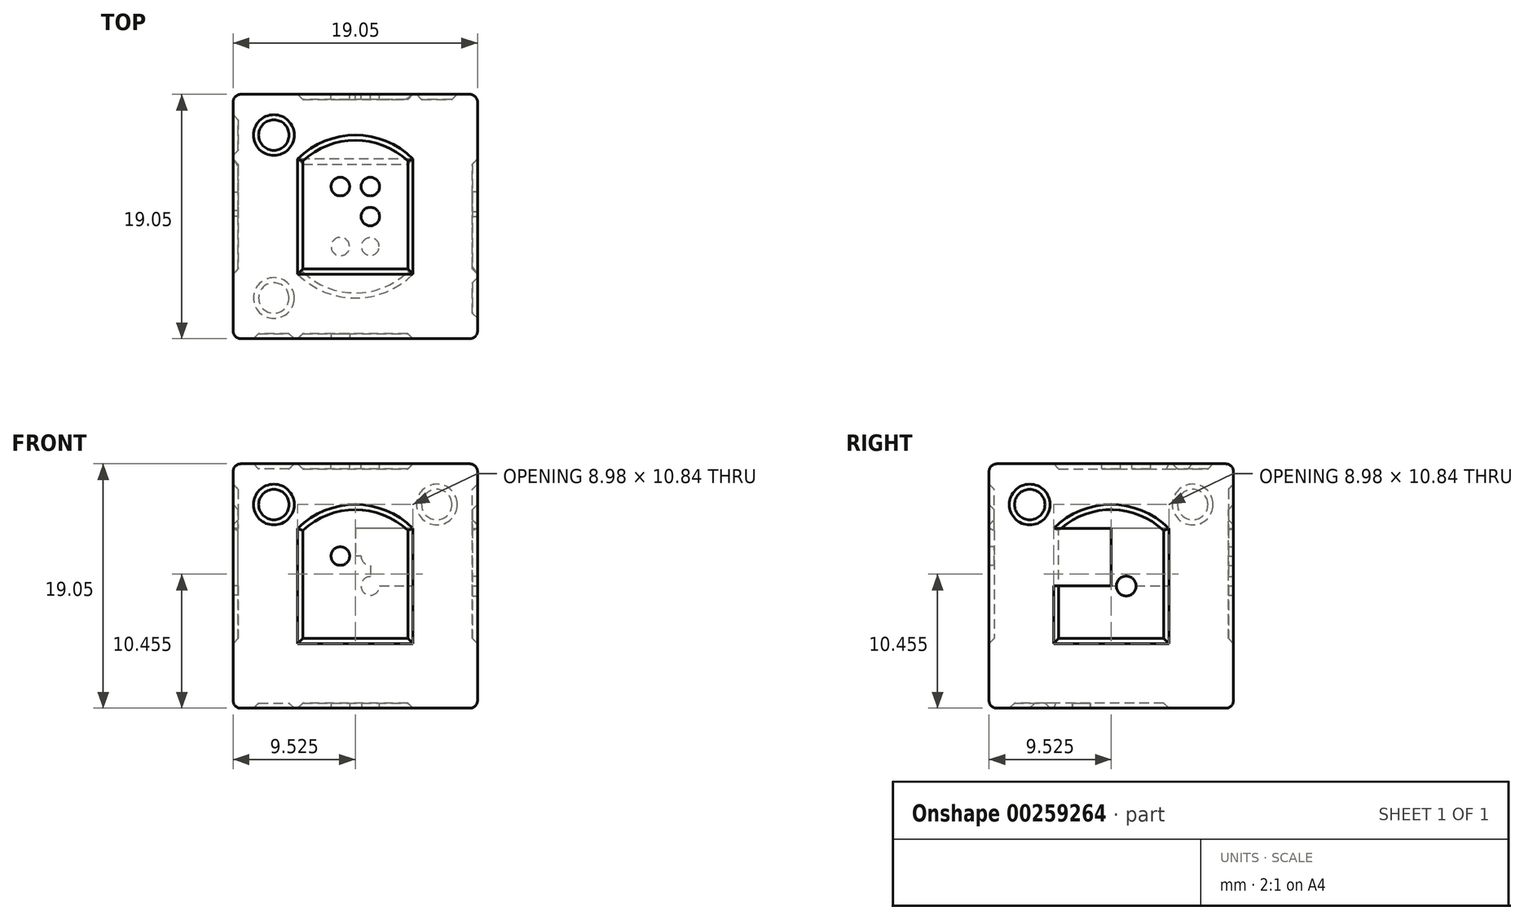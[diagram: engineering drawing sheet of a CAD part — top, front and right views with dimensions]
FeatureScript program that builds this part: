
annotation { "Feature Type Name" : "Feature", "Feature Type Description" : "" }
export const myFeature = defineFeature(function(context is Context, id is Id, definition is map)
    precondition{}
    {
        {
            assignVariable(context, id + "F0", {"name" : "d", "anyValue" : .4});
        }
        {
            assignVariable(context, id + "F1", {"name" : "r", "anyValue" : .6});
        }
        {
            var Q0;
            Q0=qCreatedBy(makeId("Front.planeOp"),FACE);
            var sketch = newSketch(context, id + "F2", { "sketchPlane" : qUnion([Q0])});
            skLineSegment(sketch, "E0.bottom", {"start": v(0, 0) * mm, "end": v(19.05, 0) * mm});
            skLineSegment(sketch, "E0.top", {"start": v(0, 19.05) * mm, "end": v(19.05, 19.05) * mm});
            skLineSegment(sketch, "E0.left", {"start": v(0, 0) * mm, "end": v(0, 19.05) * mm});
            skLineSegment(sketch, "E0.right", {"start": v(19.05, 0) * mm, "end": v(19.05, 19.05) * mm});
            skSolve(sketch);
        }
        {
            var Q0;
            Q0 = qSketchRegion(id + "F2", true);
            extrude(context, id + "F3", {"entities" : qUnion([Q0]), "depth" : 19.05 * mm});
        }
        {
            var Q0;
            Q0=makeQuery(id+"F3.opExtrude","CAP_FACE",FACE,{"disambiguationData":[OSD([sQuery(id+"F2.wireOp",EDGE,"E0.bottom"),sQuery(id+"F2.wireOp",EDGE,"E0.top"),sQuery(id+"F2.wireOp",EDGE,"E0.left"),sQuery(id+"F2.wireOp",EDGE,"E0.right")])],"isStart":false});
            var sketch = newSketch(context, id + "F4", { "sketchPlane" : qUnion([Q0])});
            skCircle(sketch, "E1", {"center": v(9.52, 9.53) * mm, "radius": 6.35 * mm});
            skPoint(sketch, "E1.centerSnap0", {"position": v(9.52, 19.05) * mm});
            skPoint(sketch, "E1.centerSnap1", {"position": v(0, 9.53) * mm});
            skCircle(sketch, "E2", {"center": v(3.18, 15.88) * mm, "radius": 1.59 * mm});
            skCircle(sketch, "E3.cCircle", {"center": v(9.52, 9.53) * mm, "radius": 6.35 * mm, "construction": true});
            skLineSegment(sketch, "E3.0", {"start": v(14.02, 14.02) * mm, "end": v(14.02, 5.03) * mm});
            skLineSegment(sketch, "E3.1", {"start": v(14.02, 5.03) * mm, "end": v(5.03, 5.03) * mm});
            skLineSegment(sketch, "E3.2", {"start": v(5.03, 5.03) * mm, "end": v(5.03, 14.02) * mm});
            skLineSegment(sketch, "E3.3", {"start": v(5.03, 14.02) * mm, "end": v(14.02, 14.02) * mm});
            skLineSegment(sketch, "E4", {"start": v(9.52, 9.53) * mm, "end": v(9.52, 14.02) * mm});
            skCircle(sketch, "E5", {"center": v(8.36, 11.86) * mm, "radius": 0.72 * mm});
            skLineSegment(sketch, "E6", {"start": v(9.52, 9.53) * mm, "end": v(5.03, 9.53) * mm});
            skSolve(sketch);
        }
        {
            var Q0;
            {var subQ4=sQuery(id+"F4.wireOp",EDGE,"E3.0");Q0=makeQuery(id+"F4.imprint","IMPRINT",FACE,{"disambiguationData":[TD([[makeQuery(id+"F4.imprint","IMPRINT",EDGE,{"derivedFrom":subQ4}),-1.0]])]});}
            var Q1;
            {var subQ0=sQuery(id+"F4.wireOp",EDGE,"E4");Q1=makeQuery(id+"F4.imprint","IMPRINT",FACE,{"disambiguationData":[TD([[makeQuery(id+"F4.imprint","IMPRINT",EDGE,{"derivedFrom":subQ0}),1.0]])]});}
            var Q2;
            {var subQ0=sQuery(id+"F4.wireOp",EDGE,"E4");Q2=makeQuery(id+"F4.imprint","IMPRINT",FACE,{"disambiguationData":[TD([[makeQuery(id+"F4.imprint","IMPRINT",EDGE,{"derivedFrom":subQ0}),-1.0]])]});}
            var Q3;
            {var subQ0=sQuery(id+"F4.wireOp",EDGE,"E3.3");var subQ4=makeQuery(id+"F4.imprint","INTERSECT",VERTEX,{"derivedFrom":[subQ0,sQuery(id+"F4.wireOp",EDGE,"E4")]});Q3=makeQuery(id+"F4.imprint","IMPRINT",FACE,{"disambiguationData":[TD([[makeQuery(id+"F4.imprint","IMPRINT",EDGE,{"disambiguationData":[TD([[subQ4,1.0]])],"derivedFrom":subQ0}),1.0]])]});}
            var Q4;
            Q4=makeQuery(id+"F4.imprint","IMPRINT",FACE,{"disambiguationData":[TD([[makeQuery(id+"F4.imprint","IMPRINT",EDGE,{"derivedFrom":sQuery(id+"F4.wireOp",EDGE,"E2")}),1.0]])]});
            extrude(context, id + "F5", {"entities" : qUnion([Q0, Q1, Q2, Q3, Q4]), "operationType" : NewBodyOperationType.REMOVE, "oppositeDirection" : true, "depth" : (getVariable(context, 'd')) * mm});
        }
        {
            var Q0;
            Q0=makeQuery(id+"F3.opExtrude","SWEPT_FACE",FACE,{"disambiguationData":[OSD([sQuery(id+"F2.wireOp",EDGE,"E0.left")])]});
            var sketch = newSketch(context, id + "F6", { "sketchPlane" : qUnion([Q0])});
            skCircle(sketch, "E7", {"center": v(9.53, 9.53) * mm, "radius": 6.35 * mm});
            skPoint(sketch, "E7.centerSnap0", {"position": v(19.05, 9.53) * mm});
            skPoint(sketch, "E7.centerSnap1", {"position": v(9.53, 19.05) * mm});
            skCircle(sketch, "E8", {"center": v(3.18, 15.88) * mm, "radius": 1.59 * mm});
            skCircle(sketch, "E9.cCircle", {"center": v(9.53, 9.53) * mm, "radius": 6.35 * mm, "construction": true});
            skLineSegment(sketch, "E9.0", {"start": v(14.02, 14.02) * mm, "end": v(14.02, 5.03) * mm});
            skLineSegment(sketch, "E9.1", {"start": v(14.02, 5.03) * mm, "end": v(5.03, 5.03) * mm});
            skLineSegment(sketch, "E9.2", {"start": v(5.03, 5.03) * mm, "end": v(5.03, 14.02) * mm});
            skLineSegment(sketch, "E9.3", {"start": v(5.03, 14.02) * mm, "end": v(14.02, 14.02) * mm});
            skLineSegment(sketch, "E10", {"start": v(9.53, 9.53) * mm, "end": v(9.53, 14.02) * mm});
            skLineSegment(sketch, "E11", {"start": v(9.53, 14.02) * mm, "end": v(9.53, 9.53) * mm});
            skLineSegment(sketch, "E12", {"start": v(9.53, 9.53) * mm, "end": v(5.03, 9.53) * mm});
            skCircle(sketch, "E13", {"center": v(8.36, 11.86) * mm, "radius": 0.72 * mm});
            skCircle(sketch, "E14", {"center": v(8.36, 9.52) * mm, "radius": 0.72 * mm});
            skSolve(sketch);
        }
        {
            var Q0;
            Q0=makeQuery(id+"F6.imprint","IMPRINT",FACE,{"disambiguationData":[TD([[makeQuery(id+"F6.imprint","IMPRINT",EDGE,{"derivedFrom":sQuery(id+"F6.wireOp",EDGE,"E8")}),1.0]])]});
            var Q1;
            {var subQ0=sQuery(id+"F6.wireOp",EDGE,"E9.3");var subQ4=makeQuery(id+"F6.imprint","INTERSECT",VERTEX,{"derivedFrom":[subQ0,sQuery(id+"F6.wireOp",EDGE,"E11")]});Q1=makeQuery(id+"F6.imprint","IMPRINT",FACE,{"disambiguationData":[TD([[makeQuery(id+"F6.imprint","IMPRINT",EDGE,{"disambiguationData":[TD([[subQ4,1.0]])],"derivedFrom":subQ0}),1.0]])]});}
            var Q2;
            {var subQ0=sQuery(id+"F6.wireOp",EDGE,"E11");Q2=makeQuery(id+"F6.imprint","IMPRINT",FACE,{"disambiguationData":[TD([[makeQuery(id+"F6.imprint","IMPRINT",EDGE,{"derivedFrom":subQ0}),-1.0]])]});}
            var Q3;
            {var subQ0=sQuery(id+"F6.wireOp",EDGE,"E11");Q3=makeQuery(id+"F6.imprint","IMPRINT",FACE,{"disambiguationData":[TD([[makeQuery(id+"F6.imprint","IMPRINT",EDGE,{"derivedFrom":subQ0}),1.0]])]});}
            var Q4;
            {var subQ9=sQuery(id+"F6.wireOp",EDGE,"E9.0");Q4=makeQuery(id+"F6.imprint","IMPRINT",FACE,{"disambiguationData":[TD([[makeQuery(id+"F6.imprint","IMPRINT",EDGE,{"derivedFrom":subQ9}),-1.0]])]});}
            extrude(context, id + "F7", {"entities" : qUnion([Q0, Q1, Q2, Q3, Q4]), "operationType" : NewBodyOperationType.REMOVE, "oppositeDirection" : true, "depth" : (getVariable(context, 'd')) * mm});
        }
        {
            var Q0;
            Q0=makeQuery(id+"F3.opExtrude","CAP_FACE",FACE,{"disambiguationData":[OSD([sQuery(id+"F2.wireOp",EDGE,"E0.bottom"),sQuery(id+"F2.wireOp",EDGE,"E0.top"),sQuery(id+"F2.wireOp",EDGE,"E0.left"),sQuery(id+"F2.wireOp",EDGE,"E0.right")])],"isStart":true});
            var sketch = newSketch(context, id + "F8", { "sketchPlane" : qUnion([Q0])});
            skCircle(sketch, "E15", {"center": v(-9.52, 9.53) * mm, "radius": 6.35 * mm});
            skPoint(sketch, "E15.centerSnap0", {"position": v(0, 9.53) * mm});
            skPoint(sketch, "E15.centerSnap1", {"position": v(-9.52, 19.05) * mm});
            skCircle(sketch, "E16.cCircle", {"center": v(-9.52, 9.53) * mm, "radius": 6.35 * mm, "construction": true});
            skLineSegment(sketch, "E16.0", {"start": v(-5.03, 14.02) * mm, "end": v(-5.03, 5.03) * mm});
            skLineSegment(sketch, "E16.1", {"start": v(-5.03, 5.03) * mm, "end": v(-14.02, 5.03) * mm});
            skLineSegment(sketch, "E16.2", {"start": v(-14.02, 5.03) * mm, "end": v(-14.02, 14.02) * mm});
            skLineSegment(sketch, "E16.3", {"start": v(-14.02, 14.02) * mm, "end": v(-5.03, 14.02) * mm});
            skLineSegment(sketch, "E17", {"start": v(-9.52, 9.52) * mm, "end": v(-14.02, 9.52) * mm});
            skLineSegment(sketch, "E18", {"start": v(-14.02, 9.52) * mm, "end": v(-9.52, 9.53) * mm});
            skLineSegment(sketch, "E19", {"start": v(-9.53, 14.02) * mm, "end": v(-9.52, 9.53) * mm});
            skCircle(sketch, "E20", {"center": v(-15.87, 15.88) * mm, "radius": 1.59 * mm});
            skCircle(sketch, "E21", {"center": v(-10.7, 11.86) * mm, "radius": 0.72 * mm});
            skCircle(sketch, "E22", {"center": v(-8.36, 11.86) * mm, "radius": 0.72 * mm});
            skCircle(sketch, "E23", {"center": v(-10.7, 9.53) * mm, "radius": 0.72 * mm});
            skLineSegment(sketch, "E24", {"start": v(-10.7, 11.86) * mm, "end": v(-10.7, 9.53) * mm});
            skLineSegment(sketch, "E25", {"start": v(-10.7, 11.86) * mm, "end": v(-8.36, 11.86) * mm});
            skSolve(sketch);
        }
        {
            var Q0;
            Q0=makeQuery(id+"F8.imprint","IMPRINT",FACE,{"disambiguationData":[TD([[makeQuery(id+"F8.imprint","IMPRINT",EDGE,{"derivedFrom":sQuery(id+"F8.wireOp",EDGE,"E20")}),1.0]])]});
            var Q1;
            {var subQ0=sQuery(id+"F8.wireOp",EDGE,"E18");var subQ1=sQuery(id+"F8.wireOp",EDGE,"E16.2");var subQ2=makeQuery(id+"F8.imprint","INTERSECT",VERTEX,{"derivedFrom":[subQ1,subQ0]});Q1=makeQuery(id+"F8.imprint","IMPRINT",FACE,{"disambiguationData":[TD([[makeQuery(id+"F8.imprint","IMPRINT",EDGE,{"disambiguationData":[TD([[subQ2,-1.0]])],"derivedFrom":subQ0}),1.0]])]});}
            var Q2;
            {var subQ0=sQuery(id+"F8.wireOp",EDGE,"E16.3");var subQ4=makeQuery(id+"F8.imprint","INTERSECT",VERTEX,{"derivedFrom":[subQ0,sQuery(id+"F8.wireOp",EDGE,"E19")]});Q2=makeQuery(id+"F8.imprint","IMPRINT",FACE,{"disambiguationData":[TD([[makeQuery(id+"F8.imprint","IMPRINT",EDGE,{"disambiguationData":[TD([[subQ4,1.0]])],"derivedFrom":subQ0}),1.0]])]});}
            var Q3;
            Q3=makeQuery(id+"F8.imprint","IMPRINT",FACE,{"disambiguationData":[TD([[makeQuery(id+"F8.imprint","IMPRINT",EDGE,{"derivedFrom":sQuery(id+"F8.wireOp",EDGE,"E22")}),-1.0]])]});
            var Q4;
            {var subQ0=sQuery(id+"F8.wireOp",EDGE,"E24");var subQ5=sQuery(id+"F8.wireOp",EDGE,"E21");var subQ6=makeQuery(id+"F8.imprint","INTERSECT",VERTEX,{"derivedFrom":[subQ5,subQ0]});Q4=makeQuery(id+"F8.imprint","IMPRINT",FACE,{"disambiguationData":[TD([[makeQuery(id+"F8.imprint","IMPRINT",EDGE,{"disambiguationData":[TD([[subQ6,-1.0]])],"derivedFrom":subQ5}),-1.0]])]});}
            var Q5;
            {var subQ8=sQuery(id+"F8.wireOp",EDGE,"E16.0");Q5=makeQuery(id+"F8.imprint","IMPRINT",FACE,{"disambiguationData":[TD([[makeQuery(id+"F8.imprint","IMPRINT",EDGE,{"derivedFrom":subQ8}),-1.0]])]});}
            extrude(context, id + "F9", {"entities" : qUnion([Q0, Q1, Q2, Q3, Q4, Q5]), "operationType" : NewBodyOperationType.REMOVE, "oppositeDirection" : true, "depth" : (getVariable(context, 'd')) * mm});
        }
        {
            var Q0;
            Q0=makeQuery(id+"F3.opExtrude","SWEPT_FACE",FACE,{"disambiguationData":[OSD([sQuery(id+"F2.wireOp",EDGE,"E0.top")])]});
            var sketch = newSketch(context, id + "F10", { "sketchPlane" : qUnion([Q0])});
            skCircle(sketch, "E26", {"center": v(9.52, -9.53) * mm, "radius": 6.35 * mm});
            skPoint(sketch, "E26.centerSnap0", {"position": v(19.05, -9.53) * mm});
            skPoint(sketch, "E26.centerSnap1", {"position": v(9.52, 0) * mm});
            skCircle(sketch, "E27", {"center": v(3.18, -3.18) * mm, "radius": 1.59 * mm});
            skCircle(sketch, "E28.cCircle", {"center": v(9.52, -9.53) * mm, "radius": 6.35 * mm, "construction": true});
            skLineSegment(sketch, "E28.0", {"start": v(14.02, -5.03) * mm, "end": v(14.02, -14.02) * mm});
            skLineSegment(sketch, "E28.1", {"start": v(14.02, -14.02) * mm, "end": v(5.03, -14.02) * mm});
            skLineSegment(sketch, "E28.2", {"start": v(5.03, -14.02) * mm, "end": v(5.03, -5.03) * mm});
            skLineSegment(sketch, "E28.3", {"start": v(5.03, -5.03) * mm, "end": v(14.02, -5.03) * mm});
            skLineSegment(sketch, "E29", {"start": v(9.52, -9.53) * mm, "end": v(5.03, -9.53) * mm});
            skCircle(sketch, "E30", {"center": v(8.36, -7.19) * mm, "radius": 0.72 * mm});
            skLineSegment(sketch, "E31", {"start": v(9.52, -9.53) * mm, "end": v(9.52, -5.03) * mm});
            skCircle(sketch, "E32", {"center": v(10.7, -7.19) * mm, "radius": 0.72 * mm});
            skLineSegment(sketch, "E33", {"start": v(9.52, -9.53) * mm, "end": v(14.02, -9.53) * mm});
            skCircle(sketch, "E34", {"center": v(10.7, -9.53) * mm, "radius": 0.72 * mm});
            skSolve(sketch);
        }
        {
            var Q0;
            {var subQ0=sQuery(id+"F10.wireOp",EDGE,"E28.3");var subQ4=makeQuery(id+"F10.imprint","INTERSECT",VERTEX,{"derivedFrom":[subQ0,sQuery(id+"F10.wireOp",EDGE,"E31")]});Q0=makeQuery(id+"F10.imprint","IMPRINT",FACE,{"disambiguationData":[TD([[makeQuery(id+"F10.imprint","IMPRINT",EDGE,{"disambiguationData":[TD([[subQ4,1.0]])],"derivedFrom":subQ0}),1.0]])]});}
            var Q1;
            Q1=makeQuery(id+"F10.imprint","IMPRINT",FACE,{"disambiguationData":[TD([[makeQuery(id+"F10.imprint","IMPRINT",EDGE,{"derivedFrom":sQuery(id+"F10.wireOp",EDGE,"E27")}),1.0]])]});
            var Q2;
            Q2=makeQuery(id+"F10.imprint","IMPRINT",FACE,{"disambiguationData":[TD([[makeQuery(id+"F10.imprint","IMPRINT",EDGE,{"derivedFrom":sQuery(id+"F10.wireOp",EDGE,"E30")}),-1.0]])]});
            var Q3;
            {var subQ0=sQuery(id+"F10.wireOp",EDGE,"E31");Q3=makeQuery(id+"F10.imprint","IMPRINT",FACE,{"disambiguationData":[TD([[makeQuery(id+"F10.imprint","IMPRINT",EDGE,{"derivedFrom":subQ0}),-1.0]])]});}
            var Q4;
            {var subQ0=sQuery(id+"F10.wireOp",EDGE,"E33");Q4=makeQuery(id+"F10.imprint","IMPRINT",FACE,{"disambiguationData":[TD([[makeQuery(id+"F10.imprint","IMPRINT",EDGE,{"derivedFrom":subQ0}),1.0]])]});}
            var Q5;
            {var subQ4=sQuery(id+"F10.wireOp",EDGE,"E28.1");Q5=makeQuery(id+"F10.imprint","IMPRINT",FACE,{"disambiguationData":[TD([[makeQuery(id+"F10.imprint","IMPRINT",EDGE,{"derivedFrom":subQ4}),-1.0]])]});}
            extrude(context, id + "F11", {"entities" : qUnion([Q0, Q1, Q2, Q3, Q4, Q5]), "operationType" : NewBodyOperationType.REMOVE, "oppositeDirection" : true, "depth" : (getVariable(context, 'd')) * mm});
        }
        {
            var Q0;
            Q0=makeQuery(id+"F3.opExtrude","SWEPT_FACE",FACE,{"disambiguationData":[OSD([sQuery(id+"F2.wireOp",EDGE,"E0.right")])]});
            var sketch = newSketch(context, id + "F12", { "sketchPlane" : qUnion([Q0])});
            skCircle(sketch, "E35", {"center": v(-9.53, 9.52) * mm, "radius": 6.35 * mm});
            skPoint(sketch, "E35.centerSnap0", {"position": v(0, 9.52) * mm});
            skPoint(sketch, "E35.centerSnap1", {"position": v(-9.53, 19.05) * mm});
            skCircle(sketch, "E36", {"center": v(-15.88, 15.87) * mm, "radius": 1.59 * mm});
            skLineSegment(sketch, "E37", {"start": v(-9.53, 9.52) * mm, "end": v(0, 19.05) * mm});
            skCircle(sketch, "E38.cCircle", {"center": v(-9.53, 9.52) * mm, "radius": 6.35 * mm, "construction": true});
            skLineSegment(sketch, "E38.0", {"start": v(-5.03, 14.02) * mm, "end": v(-5.03, 5.03) * mm});
            skLineSegment(sketch, "E38.1", {"start": v(-5.03, 5.03) * mm, "end": v(-14.02, 5.03) * mm});
            skLineSegment(sketch, "E38.2", {"start": v(-14.02, 5.03) * mm, "end": v(-14.02, 14.02) * mm});
            skLineSegment(sketch, "E38.3", {"start": v(-14.02, 14.02) * mm, "end": v(-5.03, 14.02) * mm});
            skLineSegment(sketch, "E39", {"start": v(-14.02, 9.52) * mm, "end": v(-5.03, 9.52) * mm});
            skLineSegment(sketch, "E40", {"start": v(-5.03, 9.52) * mm, "end": v(-9.53, 9.52) * mm});
            skLineSegment(sketch, "E41", {"start": v(-9.53, 14.02) * mm, "end": v(-9.53, 9.52) * mm});
            skCircle(sketch, "E42", {"center": v(-10.7, 11.86) * mm, "radius": 0.74 * mm});
            skCircle(sketch, "E43", {"center": v(-8.36, 9.52) * mm, "radius": 0.77 * mm});
            skSolve(sketch);
        }
        {
            var Q0;
            Q0=makeQuery(id+"F12.imprint","IMPRINT",FACE,{"disambiguationData":[TD([[makeQuery(id+"F12.imprint","IMPRINT",EDGE,{"derivedFrom":sQuery(id+"F12.wireOp",EDGE,"E36")}),1.0]])]});
            var Q1;
            {var subQ0=sQuery(id+"F12.wireOp",EDGE,"E38.3");var subQ4=makeQuery(id+"F12.imprint","INTERSECT",VERTEX,{"derivedFrom":[subQ0,sQuery(id+"F12.wireOp",EDGE,"E41")]});Q1=makeQuery(id+"F12.imprint","IMPRINT",FACE,{"disambiguationData":[TD([[makeQuery(id+"F12.imprint","IMPRINT",EDGE,{"disambiguationData":[TD([[subQ4,1.0]])],"derivedFrom":subQ0}),1.0]])]});}
            var Q2;
            {var subQ1=sQuery(id+"F12.wireOp",EDGE,"E39");Q2=makeQuery(id+"F12.imprint","IMPRINT",FACE,{"disambiguationData":[TD([[makeQuery(id+"F12.imprint","IMPRINT",EDGE,{"derivedFrom":subQ1}),1.0]])]});}
            var Q3;
            {var subQ0=sQuery(id+"F12.wireOp",EDGE,"E41");Q3=makeQuery(id+"F12.imprint","IMPRINT",FACE,{"disambiguationData":[TD([[makeQuery(id+"F12.imprint","IMPRINT",EDGE,{"derivedFrom":subQ0}),1.0]])]});}
            var Q4;
            {var subQ0=sQuery(id+"F12.wireOp",EDGE,"E40");var subQ5=sQuery(id+"F12.wireOp",EDGE,"E38.0");var subQ6=makeQuery(id+"F12.imprint","INTERSECT",VERTEX,{"derivedFrom":[subQ5,subQ0]});Q4=makeQuery(id+"F12.imprint","IMPRINT",FACE,{"disambiguationData":[TD([[makeQuery(id+"F12.imprint","IMPRINT",EDGE,{"disambiguationData":[TD([[subQ6,-1.0]])],"derivedFrom":subQ0}),-1.0]])]});}
            var Q5;
            {var subQ1=sQuery(id+"F12.wireOp",EDGE,"E38.1");Q5=makeQuery(id+"F12.imprint","IMPRINT",FACE,{"disambiguationData":[TD([[makeQuery(id+"F12.imprint","IMPRINT",EDGE,{"derivedFrom":subQ1}),-1.0]])]});}
            extrude(context, id + "F13", {"entities" : qUnion([Q0, Q1, Q2, Q3, Q4, Q5]), "operationType" : NewBodyOperationType.REMOVE, "oppositeDirection" : true, "depth" : (getVariable(context, 'd')) * mm});
        }
        {
            var Q0;
            Q0=makeQuery(id+"F3.opExtrude","SWEPT_FACE",FACE,{"disambiguationData":[OSD([sQuery(id+"F2.wireOp",EDGE,"E0.bottom")])]});
            var sketch = newSketch(context, id + "F14", { "sketchPlane" : qUnion([Q0])});
            skCircle(sketch, "E44", {"center": v(9.53, 9.53) * mm, "radius": 6.35 * mm});
            skPoint(sketch, "E44.centerSnap0", {"position": v(19.05, 9.53) * mm});
            skPoint(sketch, "E44.centerSnap1", {"position": v(9.53, 19.05) * mm});
            skCircle(sketch, "E45", {"center": v(3.18, 15.88) * mm, "radius": 1.59 * mm});
            skCircle(sketch, "E46.cCircle", {"center": v(9.53, 9.53) * mm, "radius": 6.35 * mm, "construction": true});
            skLineSegment(sketch, "E46.0", {"start": v(14.02, 14.02) * mm, "end": v(14.02, 5.03) * mm});
            skLineSegment(sketch, "E46.1", {"start": v(14.02, 5.03) * mm, "end": v(5.03, 5.03) * mm});
            skLineSegment(sketch, "E46.2", {"start": v(5.03, 5.03) * mm, "end": v(5.03, 14.02) * mm});
            skLineSegment(sketch, "E46.3", {"start": v(5.03, 14.02) * mm, "end": v(14.02, 14.02) * mm});
            skLineSegment(sketch, "E47", {"start": v(9.53, 9.53) * mm, "end": v(9.53, 14.02) * mm});
            skCircle(sketch, "E48", {"center": v(8.36, 11.86) * mm, "radius": 0.72 * mm});
            skCircle(sketch, "E49", {"center": v(10.7, 11.86) * mm, "radius": 0.7 * mm});
            skLineSegment(sketch, "E50", {"start": v(9.53, 9.53) * mm, "end": v(5.03, 9.53) * mm});
            skLineSegment(sketch, "E51", {"start": v(9.53, 9.53) * mm, "end": v(14.02, 9.53) * mm});
            skSolve(sketch);
        }
        {
            var Q0;
            Q0=makeQuery(id+"F14.imprint","IMPRINT",FACE,{"disambiguationData":[TD([[makeQuery(id+"F14.imprint","IMPRINT",EDGE,{"derivedFrom":sQuery(id+"F14.wireOp",EDGE,"E45")}),1.0]])]});
            var Q1;
            {var subQ0=sQuery(id+"F14.wireOp",EDGE,"E46.3");var subQ4=makeQuery(id+"F14.imprint","INTERSECT",VERTEX,{"derivedFrom":[subQ0,sQuery(id+"F14.wireOp",EDGE,"E47")]});Q1=makeQuery(id+"F14.imprint","IMPRINT",FACE,{"disambiguationData":[TD([[makeQuery(id+"F14.imprint","IMPRINT",EDGE,{"disambiguationData":[TD([[subQ4,1.0]])],"derivedFrom":subQ0}),1.0]])]});}
            var Q2;
            {var subQ3=sQuery(id+"F14.wireOp",EDGE,"E47");Q2=makeQuery(id+"F14.imprint","IMPRINT",FACE,{"disambiguationData":[TD([[makeQuery(id+"F14.imprint","IMPRINT",EDGE,{"derivedFrom":subQ3}),1.0]])]});}
            var Q3;
            {var subQ3=sQuery(id+"F14.wireOp",EDGE,"E47");Q3=makeQuery(id+"F14.imprint","IMPRINT",FACE,{"disambiguationData":[TD([[makeQuery(id+"F14.imprint","IMPRINT",EDGE,{"derivedFrom":subQ3}),-1.0]])]});}
            var Q4;
            {var subQ1=sQuery(id+"F14.wireOp",EDGE,"E46.1");Q4=makeQuery(id+"F14.imprint","IMPRINT",FACE,{"disambiguationData":[TD([[makeQuery(id+"F14.imprint","IMPRINT",EDGE,{"derivedFrom":subQ1}),-1.0]])]});}
            extrude(context, id + "F15", {"entities" : qUnion([Q0, Q1, Q2, Q3, Q4]), "operationType" : NewBodyOperationType.REMOVE, "oppositeDirection" : true, "depth" : (getVariable(context, 'd')) * mm});
        }
        {
            var Q0;
            Q0=makeQuery(id+"F11.boolean.opBoolean","COPY",EDGE,{"derivedFrom":makeQuery(id+"F11.opExtrude","CAP_EDGE",EDGE,{"disambiguationData":[OSD([sQuery(id+"F10.wireOp",EDGE,"E27")])],"isStart":false})});
            var Q1;
            Q1=makeQuery(id+"F7.boolean.opBoolean","COPY",EDGE,{"derivedFrom":makeQuery(id+"F7.opExtrude","CAP_EDGE",EDGE,{"disambiguationData":[OSD([sQuery(id+"F6.wireOp",EDGE,"E8")])],"isStart":false})});
            var Q2;
            Q2=makeQuery(id+"F9.boolean.opBoolean","COPY",EDGE,{"derivedFrom":makeQuery(id+"F9.opExtrude","CAP_EDGE",EDGE,{"disambiguationData":[OSD([sQuery(id+"F8.wireOp",EDGE,"E20")])],"isStart":false})});
            var Q3;
            Q3=makeQuery(id+"F13.boolean.opBoolean","COPY",EDGE,{"derivedFrom":makeQuery(id+"F13.opExtrude","CAP_EDGE",EDGE,{"disambiguationData":[OSD([sQuery(id+"F12.wireOp",EDGE,"E36")])],"isStart":false})});
            var Q4;
            Q4=makeQuery(id+"F5.boolean.opBoolean","COPY",EDGE,{"derivedFrom":makeQuery(id+"F5.opExtrude","CAP_EDGE",EDGE,{"disambiguationData":[OSD([sQuery(id+"F4.wireOp",EDGE,"E2")])],"isStart":false})});
            var Q5;
            Q5=makeQuery(id+"F15.boolean.opBoolean","COPY",EDGE,{"derivedFrom":makeQuery(id+"F15.opExtrude","CAP_EDGE",EDGE,{"disambiguationData":[OSD([sQuery(id+"F14.wireOp",EDGE,"E45")])],"isStart":false})});
            chamfer(context, id + "F16", {"entities" : qUnion([Q0, Q1, Q2, Q3, Q4, Q5]), "width" : (getVariable(context, 'd')) * mm, "tangentPropagation" : true});
        }
        {
            var Q0;
            Q0=makeQuery(id+"F3.opExtrude","CAP_EDGE",EDGE,{"disambiguationData":[OSD([sQuery(id+"F2.wireOp",EDGE,"E0.top")])],"isStart":false});
            var Q1;
            Q1=makeQuery(id+"F3.opExtrude","CAP_EDGE",EDGE,{"disambiguationData":[OSD([sQuery(id+"F2.wireOp",EDGE,"E0.right")])],"isStart":false});
            var Q2;
            Q2=makeQuery(id+"F3.opExtrude","CAP_EDGE",EDGE,{"disambiguationData":[OSD([sQuery(id+"F2.wireOp",EDGE,"E0.left")])],"isStart":false});
            var Q3;
            Q3=makeQuery(id+"F3.opExtrude","CAP_EDGE",EDGE,{"disambiguationData":[OSD([sQuery(id+"F2.wireOp",EDGE,"E0.bottom")])],"isStart":false});
            var Q4;
            Q4=makeQuery(id+"F3.opExtrude","CAP_EDGE",EDGE,{"disambiguationData":[OSD([sQuery(id+"F2.wireOp",EDGE,"E0.top")])],"isStart":true});
            var Q5;
            Q5=makeQuery(id+"F3.opExtrude","CAP_EDGE",EDGE,{"disambiguationData":[OSD([sQuery(id+"F2.wireOp",EDGE,"E0.left")])],"isStart":true});
            var Q6;
            Q6=makeQuery(id+"F3.opExtrude","CAP_EDGE",EDGE,{"disambiguationData":[OSD([sQuery(id+"F2.wireOp",EDGE,"E0.bottom")])],"isStart":true});
            var Q7;
            Q7=makeQuery(id+"F3.opExtrude","CAP_EDGE",EDGE,{"disambiguationData":[OSD([sQuery(id+"F2.wireOp",EDGE,"E0.right")])],"isStart":true});
            var Q8;
            Q8=makeQuery(id+"F3.opExtrude","SWEPT_EDGE",EDGE,{"disambiguationData":[OSD([sQuery(id+"F2.wireOp",EDGE,"E0.top"),sQuery(id+"F2.wireOp",EDGE,"E0.right")])]});
            var Q9;
            Q9=makeQuery(id+"F3.opExtrude","SWEPT_EDGE",EDGE,{"disambiguationData":[OSD([sQuery(id+"F2.wireOp",EDGE,"E0.top"),sQuery(id+"F2.wireOp",EDGE,"E0.left")])]});
            var Q10;
            Q10=makeQuery(id+"F3.opExtrude","SWEPT_EDGE",EDGE,{"disambiguationData":[OSD([sQuery(id+"F2.wireOp",EDGE,"E0.bottom"),sQuery(id+"F2.wireOp",EDGE,"E0.left")])]});
            var Q11;
            Q11=makeQuery(id+"F3.opExtrude","SWEPT_EDGE",EDGE,{"disambiguationData":[OSD([sQuery(id+"F2.wireOp",EDGE,"E0.bottom"),sQuery(id+"F2.wireOp",EDGE,"E0.right")])]});
            fillet(context, id + "F17", {"entities" : qUnion([Q0, Q1, Q2, Q3, Q4, Q5, Q6, Q7, Q8, Q9, Q10, Q11]), "radius" : (getVariable(context, 'r')) * mm, "tangentPropagation" : true, "allowEdgeOverflow" : false});
        }
        {
            var Q0;
            Q0=makeQuery(id+"F5.boolean.opBoolean","COPY",EDGE,{"derivedFrom":makeQuery(id+"F5.opExtrude","CAP_EDGE",EDGE,{"disambiguationData":[OSD([sQuery(id+"F4.wireOp",EDGE,"E1")])],"isStart":false})});
            var Q1;
            Q1=makeQuery(id+"F5.boolean.opBoolean","COPY",EDGE,{"derivedFrom":makeQuery(id+"F5.opExtrude","CAP_EDGE",EDGE,{"disambiguationData":[OSD([sQuery(id+"F4.wireOp",EDGE,"E3.0")])],"isStart":false})});
            var Q2;
            Q2=makeQuery(id+"F5.boolean.opBoolean","COPY",EDGE,{"derivedFrom":makeQuery(id+"F5.opExtrude","CAP_EDGE",EDGE,{"disambiguationData":[OSD([sQuery(id+"F4.wireOp",EDGE,"E3.1")])],"isStart":false})});
            var Q3;
            Q3=makeQuery(id+"F5.boolean.opBoolean","COPY",EDGE,{"derivedFrom":makeQuery(id+"F5.opExtrude","CAP_EDGE",EDGE,{"disambiguationData":[OSD([sQuery(id+"F4.wireOp",EDGE,"E3.2")])],"isStart":false})});
            chamfer(context, id + "F18", {"entities" : qUnion([Q0, Q1, Q2, Q3]), "width" : (getVariable(context, 'd')) * mm, "tangentPropagation" : true});
        }
        {
            var Q0;
            Q0=makeQuery(id+"F7.boolean.opBoolean","COPY",EDGE,{"derivedFrom":makeQuery(id+"F7.opExtrude","CAP_EDGE",EDGE,{"disambiguationData":[OSD([sQuery(id+"F6.wireOp",EDGE,"E7")])],"isStart":false})});
            var Q1;
            Q1=makeQuery(id+"F7.boolean.opBoolean","COPY",EDGE,{"derivedFrom":makeQuery(id+"F7.opExtrude","CAP_EDGE",EDGE,{"disambiguationData":[OSD([sQuery(id+"F6.wireOp",EDGE,"E9.0")])],"isStart":false})});
            var Q2;
            Q2=makeQuery(id+"F7.boolean.opBoolean","COPY",EDGE,{"derivedFrom":makeQuery(id+"F7.opExtrude","CAP_EDGE",EDGE,{"disambiguationData":[OSD([sQuery(id+"F6.wireOp",EDGE,"E9.1")])],"isStart":false})});
            var Q3;
            Q3=makeQuery(id+"F7.boolean.opBoolean","COPY",EDGE,{"derivedFrom":makeQuery(id+"F7.opExtrude","CAP_EDGE",EDGE,{"disambiguationData":[OSD([sQuery(id+"F6.wireOp",EDGE,"E9.2")])],"isStart":false})});
            chamfer(context, id + "F19", {"entities" : qUnion([Q0, Q1, Q2, Q3]), "width" : (getVariable(context, 'd')) * mm, "tangentPropagation" : true});
        }
        {
            var Q0;
            Q0=makeQuery(id+"F15.boolean.opBoolean","COPY",EDGE,{"derivedFrom":makeQuery(id+"F15.opExtrude","CAP_EDGE",EDGE,{"disambiguationData":[OSD([sQuery(id+"F14.wireOp",EDGE,"E44")])],"isStart":false})});
            var Q1;
            Q1=makeQuery(id+"F15.boolean.opBoolean","COPY",EDGE,{"derivedFrom":makeQuery(id+"F15.opExtrude","CAP_EDGE",EDGE,{"disambiguationData":[OSD([sQuery(id+"F14.wireOp",EDGE,"E46.0")])],"isStart":false})});
            var Q2;
            Q2=makeQuery(id+"F15.boolean.opBoolean","COPY",EDGE,{"derivedFrom":makeQuery(id+"F15.opExtrude","CAP_EDGE",EDGE,{"disambiguationData":[OSD([sQuery(id+"F14.wireOp",EDGE,"E46.1")])],"isStart":false})});
            var Q3;
            Q3=makeQuery(id+"F15.boolean.opBoolean","COPY",EDGE,{"derivedFrom":makeQuery(id+"F15.opExtrude","CAP_EDGE",EDGE,{"disambiguationData":[OSD([sQuery(id+"F14.wireOp",EDGE,"E46.2")])],"isStart":false})});
            chamfer(context, id + "F20", {"entities" : qUnion([Q0, Q1, Q2, Q3]), "width" : (getVariable(context, 'd')) * mm, "tangentPropagation" : true});
        }
        {
            var Q0;
            Q0=makeQuery(id+"F11.boolean.opBoolean","COPY",EDGE,{"derivedFrom":makeQuery(id+"F11.opExtrude","CAP_EDGE",EDGE,{"disambiguationData":[OSD([sQuery(id+"F10.wireOp",EDGE,"E26")])],"isStart":false})});
            var Q1;
            Q1=makeQuery(id+"F11.boolean.opBoolean","COPY",EDGE,{"derivedFrom":makeQuery(id+"F11.opExtrude","CAP_EDGE",EDGE,{"disambiguationData":[OSD([sQuery(id+"F10.wireOp",EDGE,"E28.0")])],"isStart":false})});
            var Q2;
            Q2=makeQuery(id+"F11.boolean.opBoolean","COPY",EDGE,{"derivedFrom":makeQuery(id+"F11.opExtrude","CAP_EDGE",EDGE,{"disambiguationData":[OSD([sQuery(id+"F10.wireOp",EDGE,"E28.1")])],"isStart":false})});
            var Q3;
            Q3=makeQuery(id+"F11.boolean.opBoolean","COPY",EDGE,{"derivedFrom":makeQuery(id+"F11.opExtrude","CAP_EDGE",EDGE,{"disambiguationData":[OSD([sQuery(id+"F10.wireOp",EDGE,"E28.2")])],"isStart":false})});
            chamfer(context, id + "F21", {"entities" : qUnion([Q0, Q1, Q2, Q3]), "width" : (getVariable(context, 'd')) * mm, "tangentPropagation" : true});
        }
        {
            var Q0;
            Q0=makeQuery(id+"F13.boolean.opBoolean","COPY",EDGE,{"derivedFrom":makeQuery(id+"F13.opExtrude","CAP_EDGE",EDGE,{"disambiguationData":[OSD([sQuery(id+"F12.wireOp",EDGE,"E38.0")])],"isStart":false})});
            var Q1;
            Q1=makeQuery(id+"F13.boolean.opBoolean","COPY",EDGE,{"derivedFrom":makeQuery(id+"F13.opExtrude","CAP_EDGE",EDGE,{"disambiguationData":[OSD([sQuery(id+"F12.wireOp",EDGE,"E38.1")])],"isStart":false})});
            var Q2;
            Q2=makeQuery(id+"F13.boolean.opBoolean","COPY",EDGE,{"derivedFrom":makeQuery(id+"F13.opExtrude","CAP_EDGE",EDGE,{"disambiguationData":[OSD([sQuery(id+"F12.wireOp",EDGE,"E38.2")])],"isStart":false})});
            var Q3;
            Q3=makeQuery(id+"F13.boolean.opBoolean","COPY",EDGE,{"derivedFrom":makeQuery(id+"F13.opExtrude","CAP_EDGE",EDGE,{"disambiguationData":[OSD([sQuery(id+"F12.wireOp",EDGE,"E35")])],"isStart":false})});
            chamfer(context, id + "F22", {"entities" : qUnion([Q0, Q1, Q2, Q3]), "width" : (getVariable(context, 'd')) * mm, "tangentPropagation" : true});
        }
        {
            var Q0;
            Q0=makeQuery(id+"F9.boolean.opBoolean","COPY",EDGE,{"derivedFrom":makeQuery(id+"F9.opExtrude","CAP_EDGE",EDGE,{"disambiguationData":[OSD([sQuery(id+"F8.wireOp",EDGE,"E15")])],"isStart":false})});
            var Q1;
            Q1=makeQuery(id+"F9.boolean.opBoolean","COPY",EDGE,{"derivedFrom":makeQuery(id+"F9.opExtrude","CAP_EDGE",EDGE,{"disambiguationData":[OSD([sQuery(id+"F8.wireOp",EDGE,"E16.0")])],"isStart":false})});
            var Q2;
            Q2=makeQuery(id+"F9.boolean.opBoolean","COPY",EDGE,{"derivedFrom":makeQuery(id+"F9.opExtrude","CAP_EDGE",EDGE,{"disambiguationData":[OSD([sQuery(id+"F8.wireOp",EDGE,"E16.1")])],"isStart":false})});
            var Q3;
            Q3=makeQuery(id+"F9.boolean.opBoolean","COPY",EDGE,{"derivedFrom":makeQuery(id+"F9.opExtrude","CAP_EDGE",EDGE,{"disambiguationData":[OSD([sQuery(id+"F8.wireOp",EDGE,"E16.2")])],"isStart":false})});
            chamfer(context, id + "F23", {"entities" : qUnion([Q0, Q1, Q2, Q3]), "width" : (getVariable(context, 'd')) * mm, "tangentPropagation" : true});
        }
    });
